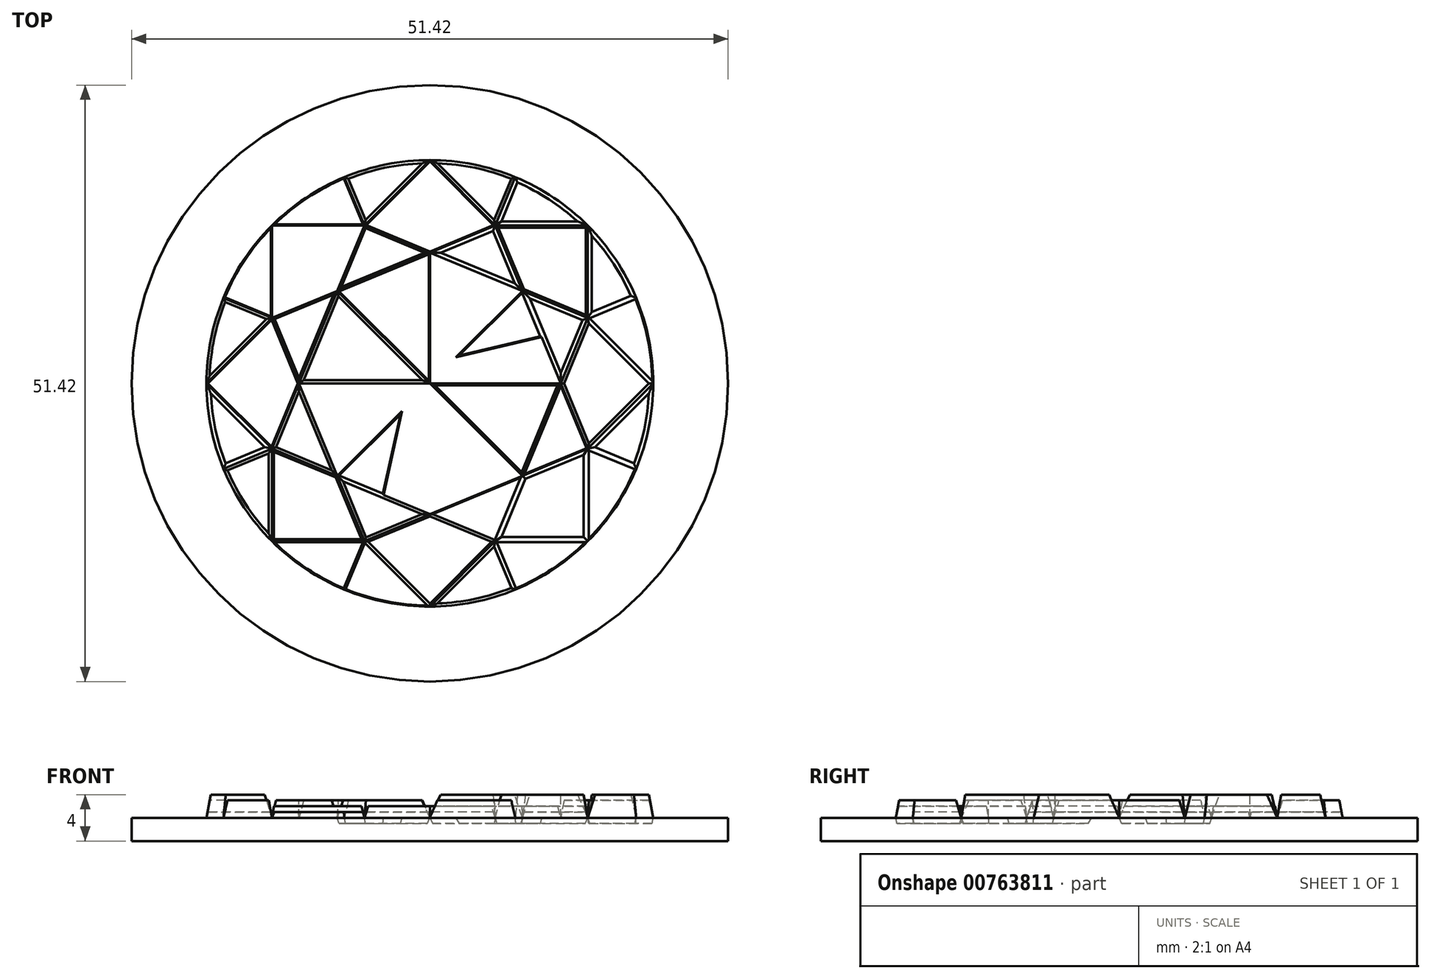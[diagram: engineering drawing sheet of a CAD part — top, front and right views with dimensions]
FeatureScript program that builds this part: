
annotation { "Feature Type Name" : "Feature", "Feature Type Description" : "" }
export const myFeature = defineFeature(function(context is Context, id is Id, definition is map)
    precondition{}
    {
        {
            var Q0;
            Q0=qCreatedBy(makeId("Top.planeOp"),FACE);
            var sketch = newSketch(context, id + "F0", { "sketchPlane" : qUnion([Q0])});
            skCircle(sketch, "E0", {"center": v(0, 0) * mm, "radius": 25.71 * mm});
            skSolve(sketch);
        }
        {
            var Q0;
            Q0 = qSketchRegion(id + "F0", true);
            extrude(context, id + "F1", {"entities" : qUnion([Q0]), "oppositeDirection" : true, "depth" : 2 * mm, "offsetDistance" : 25 * mm});
        }
        {
            var Q0;
            Q0=qCreatedBy(makeId("Top.planeOp"),FACE);
            var sketch = newSketch(context, id + "F2", { "sketchPlane" : qUnion([Q0])});
            skCircle(sketch, "E1", {"center": v(0, 0) * mm, "radius": 19.25 * mm});
            skCircle(sketch, "E2", {"center": v(0, 0) * mm, "radius": 25 * mm});
            skCircle(sketch, "E3.cCircle", {"center": v(0, 0) * mm, "radius": 14.73 * mm, "construction": true});
            skLineSegment(sketch, "E3.0", {"start": v(5.64, 13.61) * mm, "end": v(13.61, -5.64) * mm});
            skLineSegment(sketch, "E3.1", {"start": v(13.61, -5.64) * mm, "end": v(-5.64, -13.61) * mm});
            skLineSegment(sketch, "E3.2", {"start": v(-5.64, -13.61) * mm, "end": v(-13.61, 5.64) * mm});
            skLineSegment(sketch, "E3.3", {"start": v(-13.61, 5.64) * mm, "end": v(5.64, 13.61) * mm});
            skCircle(sketch, "E4.cCircle", {"center": v(0, 0) * mm, "radius": 19.25 * mm, "construction": true});
            skLineSegment(sketch, "E4.0", {"start": v(0, 19.25) * mm, "end": v(19.25, 0) * mm});
            skLineSegment(sketch, "E4.1", {"start": v(19.25, 0) * mm, "end": v(0, -19.25) * mm});
            skLineSegment(sketch, "E4.2", {"start": v(0, -19.25) * mm, "end": v(-19.25, 0) * mm});
            skLineSegment(sketch, "E4.3", {"start": v(-19.25, 0) * mm, "end": v(0, 19.25) * mm});
            skLineSegment(sketch, "E5.0", {"start": v(-13.61, 13.61) * mm, "end": v(13.61, 13.61) * mm});
            skLineSegment(sketch, "E5.1", {"start": v(13.61, 13.61) * mm, "end": v(13.61, -13.61) * mm});
            skLineSegment(sketch, "E5.2", {"start": v(13.61, -13.61) * mm, "end": v(-13.61, -13.61) * mm});
            skLineSegment(sketch, "E5.3", {"start": v(-13.61, -13.61) * mm, "end": v(-13.61, 13.61) * mm});
            skLineSegment(sketch, "E6.0", {"start": v(-5.64, 13.61) * mm, "end": v(13.61, 5.64) * mm});
            skLineSegment(sketch, "E6.1", {"start": v(13.61, 5.64) * mm, "end": v(5.64, -13.61) * mm});
            skLineSegment(sketch, "E6.2", {"start": v(5.64, -13.61) * mm, "end": v(-13.61, -5.64) * mm});
            skLineSegment(sketch, "E6.3", {"start": v(-13.61, -5.64) * mm, "end": v(-5.64, 13.61) * mm});
            skLineSegment(sketch, "E7", {"start": v(7.97, -7.97) * mm, "end": v(-7.97, 7.97) * mm});
            skLineSegment(sketch, "E8", {"start": v(-7.97, -7.97) * mm, "end": v(7.97, 7.97) * mm});
            skLineSegment(sketch, "E9", {"start": v(13.61, -5.64) * mm, "end": v(17.78, -7.37) * mm});
            skLineSegment(sketch, "E10", {"start": v(7.37, -17.78) * mm, "end": v(5.64, -13.61) * mm});
            skLineSegment(sketch, "E11", {"start": v(-7.37, -17.78) * mm, "end": v(-5.64, -13.61) * mm});
            skLineSegment(sketch, "E12", {"start": v(-13.61, -5.64) * mm, "end": v(-17.78, -7.37) * mm});
            skLineSegment(sketch, "E13", {"start": v(-13.61, 5.64) * mm, "end": v(-17.78, 7.37) * mm});
            skLineSegment(sketch, "E14", {"start": v(-5.64, 13.61) * mm, "end": v(-7.37, 17.78) * mm});
            skLineSegment(sketch, "E15", {"start": v(5.64, 13.61) * mm, "end": v(7.37, 17.78) * mm});
            skLineSegment(sketch, "E16", {"start": v(13.61, 5.64) * mm, "end": v(17.78, 7.37) * mm});
            skLineSegment(sketch, "E17", {"start": v(-2.39, -2.39) * mm, "end": v(-3.99, -9.63) * mm});
            skLineSegment(sketch, "E18", {"start": v(2.25, 2.25) * mm, "end": v(9.62, 3.99) * mm});
            skLineSegment(sketch, "E19", {"start": v(-25, 0) * mm, "end": v(-19.25, 0) * mm});
            skLineSegment(sketch, "E20", {"start": v(19.25, 0) * mm, "end": v(25, 0) * mm});
            skLineSegment(sketch, "E21", {"start": v(0, 0) * mm, "end": v(11.28, 0) * mm});
            skLineSegment(sketch, "E22", {"start": v(0, 0) * mm, "end": v(0, 11.28) * mm});
            skLineSegment(sketch, "E23", {"start": v(0, 0) * mm, "end": v(-11.28, 0) * mm});
            skSolve(sketch);
        }
        {
            var Q0;
            {var subQ3=sQuery(id+"F2.wireOp",EDGE,"E13");Q0=makeQuery(id+"F2.imprint","IMPRINT",FACE,{"disambiguationData":[TD([[makeQuery(id+"F2.imprint","IMPRINT",EDGE,{"derivedFrom":subQ3}),-1.0]])]});}
            var Q1;
            {var subQ3=sQuery(id+"F2.wireOp",EDGE,"E14");Q1=makeQuery(id+"F2.imprint","IMPRINT",FACE,{"disambiguationData":[TD([[makeQuery(id+"F2.imprint","IMPRINT",EDGE,{"derivedFrom":subQ3}),1.0]])]});}
            var Q2;
            {var subQ1=sQuery(id+"F2.wireOp",EDGE,"E4.0");var subQ3=sQuery(id+"F2.wireOp",EDGE,"E4.3");var subQ4=makeQuery(id+"F2.imprint","INTERSECT",VERTEX,{"derivedFrom":[sQuery(id+"F2.wireOp",EDGE,"E1"),subQ1,subQ3]});Q2=makeQuery(id+"F2.imprint","IMPRINT",FACE,{"disambiguationData":[TD([[makeQuery(id+"F2.imprint","IMPRINT",EDGE,{"disambiguationData":[TD([[subQ4,-1.0]])],"derivedFrom":subQ1}),-1.0]])]});}
            var Q3;
            {var subQ1=sQuery(id+"F2.wireOp",EDGE,"E3.3");var subQ3=sQuery(id+"F2.wireOp",EDGE,"E6.0");var subQ4=makeQuery(id+"F2.imprint","INTERSECT",VERTEX,{"derivedFrom":[subQ1,subQ3,sQuery(id+"F2.wireOp",EDGE,"E22")]});Q3=makeQuery(id+"F2.imprint","IMPRINT",FACE,{"disambiguationData":[TD([[makeQuery(id+"F2.imprint","IMPRINT",EDGE,{"disambiguationData":[TD([[subQ4,-1.0]])],"derivedFrom":subQ1}),1.0]])]});}
            var Q4;
            {var subQ3=sQuery(id+"F2.wireOp",EDGE,"E22");Q4=makeQuery(id+"F2.imprint","IMPRINT",FACE,{"disambiguationData":[TD([[makeQuery(id+"F2.imprint","IMPRINT",EDGE,{"derivedFrom":subQ3}),1.0]])]});}
            var Q5;
            {var subQ0=sQuery(id+"F2.wireOp",EDGE,"E3.1");var subQ3=sQuery(id+"F2.wireOp",EDGE,"E6.1");var subQ5=makeQuery(id+"F2.imprint","INTERSECT",VERTEX,{"derivedFrom":[subQ0,subQ3,sQuery(id+"F2.wireOp",EDGE,"E7")]});Q5=makeQuery(id+"F2.imprint","IMPRINT",FACE,{"disambiguationData":[TD([[makeQuery(id+"F2.imprint","IMPRINT",EDGE,{"disambiguationData":[TD([[subQ5,1.0]])],"derivedFrom":subQ3}),1.0]])]});}
            var Q6;
            {var subQ3=sQuery(id+"F2.wireOp",EDGE,"E11");Q6=makeQuery(id+"F2.imprint","IMPRINT",FACE,{"disambiguationData":[TD([[makeQuery(id+"F2.imprint","IMPRINT",EDGE,{"derivedFrom":subQ3}),1.0]])]});}
            var Q7;
            {var subQ1=sQuery(id+"F2.wireOp",EDGE,"E3.2");var subQ3=sQuery(id+"F2.wireOp",EDGE,"E6.3");var subQ4=makeQuery(id+"F2.imprint","INTERSECT",VERTEX,{"derivedFrom":[subQ1,subQ3,sQuery(id+"F2.wireOp",EDGE,"E23")]});Q7=makeQuery(id+"F2.imprint","IMPRINT",FACE,{"disambiguationData":[TD([[makeQuery(id+"F2.imprint","IMPRINT",EDGE,{"disambiguationData":[TD([[subQ4,-1.0]])],"derivedFrom":subQ1}),1.0]])]});}
            var Q8;
            {var subQ0=sQuery(id+"F2.wireOp",EDGE,"E4.3");var subQ1=sQuery(id+"F2.wireOp",EDGE,"E4.2");var subQ2=makeQuery(id+"F2.imprint","INTERSECT",VERTEX,{"derivedFrom":[sQuery(id+"F2.wireOp",EDGE,"E1"),subQ1,subQ0,sQuery(id+"F2.wireOp",EDGE,"E19")]});Q8=makeQuery(id+"F2.imprint","IMPRINT",FACE,{"disambiguationData":[TD([[makeQuery(id+"F2.imprint","IMPRINT",EDGE,{"disambiguationData":[TD([[subQ2,1.0]])],"derivedFrom":subQ1}),-1.0]])]});}
            extrude(context, id + "F3", {"entities" : qUnion([Q0, Q1, Q2, Q3, Q4, Q5, Q6, Q7, Q8]), "operationType" : NewBodyOperationType.ADD, "flatOperationType" : FlatOperationType.REMOVE, "depth" : 0.5 * mm, "offsetDistance" : 25 * mm, "hasDraft" : true, "draftAngle" : 10 * degree, "draftPullDirection" : true, "domain" : OperationDomain.MODEL});
        }
        {
            var Q0;
            {var subQ1=sQuery(id+"F2.wireOp",EDGE,"E3.1");var subQ3=sQuery(id+"F2.wireOp",EDGE,"E6.2");var subQ4=makeQuery(id+"F2.imprint","INTERSECT",VERTEX,{"derivedFrom":[subQ1,subQ3]});Q0=makeQuery(id+"F2.imprint","IMPRINT",FACE,{"disambiguationData":[TD([[makeQuery(id+"F2.imprint","IMPRINT",EDGE,{"disambiguationData":[TD([[subQ4,-1.0]])],"derivedFrom":subQ1}),1.0]])]});}
            var Q1;
            {var subQ0=sQuery(id+"F2.wireOp",EDGE,"E4.2");var subQ1=sQuery(id+"F2.wireOp",EDGE,"E4.1");var subQ2=makeQuery(id+"F2.imprint","INTERSECT",VERTEX,{"derivedFrom":[sQuery(id+"F2.wireOp",EDGE,"E1"),subQ1,subQ0]});Q1=makeQuery(id+"F2.imprint","IMPRINT",FACE,{"disambiguationData":[TD([[makeQuery(id+"F2.imprint","IMPRINT",EDGE,{"disambiguationData":[TD([[subQ2,1.0]])],"derivedFrom":subQ1}),-1.0]])]});}
            var Q2;
            {var subQ0=sQuery(id+"F2.wireOp",EDGE,"E5.2");var subQ3=sQuery(id+"F2.wireOp",EDGE,"E5.3");var subQ5=makeQuery(id+"F2.imprint","INTERSECT",VERTEX,{"derivedFrom":[sQuery(id+"F2.wireOp",EDGE,"E1"),subQ0,subQ3]});Q2=makeQuery(id+"F2.imprint","IMPRINT",FACE,{"disambiguationData":[TD([[makeQuery(id+"F2.imprint","IMPRINT",EDGE,{"disambiguationData":[TD([[subQ5,1.0]])],"derivedFrom":subQ0}),-1.0]])]});}
            var Q3;
            {var subQ1=sQuery(id+"F2.wireOp",EDGE,"E3.2");var subQ3=sQuery(id+"F2.wireOp",EDGE,"E6.2");var subQ4=makeQuery(id+"F2.imprint","INTERSECT",VERTEX,{"derivedFrom":[subQ1,subQ3,sQuery(id+"F2.wireOp",EDGE,"E8")]});Q3=makeQuery(id+"F2.imprint","IMPRINT",FACE,{"disambiguationData":[TD([[makeQuery(id+"F2.imprint","IMPRINT",EDGE,{"disambiguationData":[TD([[subQ4,1.0]])],"derivedFrom":subQ1}),1.0]])]});}
            var Q4;
            {var subQ3=sQuery(id+"F2.wireOp",EDGE,"E21");Q4=makeQuery(id+"F2.imprint","IMPRINT",FACE,{"disambiguationData":[TD([[makeQuery(id+"F2.imprint","IMPRINT",EDGE,{"derivedFrom":subQ3}),-1.0]])]});}
            var Q5;
            {var subQ0=sQuery(id+"F2.wireOp",EDGE,"E5.0");var subQ3=sQuery(id+"F2.wireOp",EDGE,"E5.1");var subQ5=makeQuery(id+"F2.imprint","INTERSECT",VERTEX,{"derivedFrom":[sQuery(id+"F2.wireOp",EDGE,"E1"),subQ0,subQ3]});Q5=makeQuery(id+"F2.imprint","IMPRINT",FACE,{"disambiguationData":[TD([[makeQuery(id+"F2.imprint","IMPRINT",EDGE,{"disambiguationData":[TD([[subQ5,1.0]])],"derivedFrom":subQ0}),-1.0]])]});}
            var Q6;
            {var subQ1=sQuery(id+"F2.wireOp",EDGE,"E3.0");var subQ3=sQuery(id+"F2.wireOp",EDGE,"E6.0");var subQ4=makeQuery(id+"F2.imprint","INTERSECT",VERTEX,{"derivedFrom":[subQ1,subQ3,sQuery(id+"F2.wireOp",EDGE,"E8")]});Q6=makeQuery(id+"F2.imprint","IMPRINT",FACE,{"disambiguationData":[TD([[makeQuery(id+"F2.imprint","IMPRINT",EDGE,{"disambiguationData":[TD([[subQ4,1.0]])],"derivedFrom":subQ1}),1.0]])]});}
            var Q7;
            {var subQ0=sQuery(id+"F2.wireOp",EDGE,"E6.3");var subQ1=sQuery(id+"F2.wireOp",EDGE,"E3.3");var subQ2=makeQuery(id+"F2.imprint","INTERSECT",VERTEX,{"derivedFrom":[subQ1,subQ0,sQuery(id+"F2.wireOp",EDGE,"E7")]});Q7=makeQuery(id+"F2.imprint","IMPRINT",FACE,{"disambiguationData":[TD([[makeQuery(id+"F2.imprint","IMPRINT",EDGE,{"disambiguationData":[TD([[subQ2,-1.0]])],"derivedFrom":subQ1}),1.0]])]});}
            var Q8;
            {var subQ0=sQuery(id+"F2.wireOp",EDGE,"E3.3");var subQ3=sQuery(id+"F2.wireOp",EDGE,"E6.3");var subQ5=makeQuery(id+"F2.imprint","INTERSECT",VERTEX,{"derivedFrom":[subQ0,subQ3,sQuery(id+"F2.wireOp",EDGE,"E7")]});Q8=makeQuery(id+"F2.imprint","IMPRINT",FACE,{"disambiguationData":[TD([[makeQuery(id+"F2.imprint","IMPRINT",EDGE,{"disambiguationData":[TD([[subQ5,1.0]])],"derivedFrom":subQ3}),1.0]])]});}
            extrude(context, id + "F4", {"entities" : qUnion([Q0, Q1, Q2, Q3, Q4, Q5, Q6, Q7, Q8]), "operationType" : NewBodyOperationType.ADD, "flatOperationType" : FlatOperationType.REMOVE, "depth" : 1 * mm, "offsetDistance" : 25 * mm, "hasDraft" : true, "draftAngle" : 10 * degree, "draftPullDirection" : true, "domain" : OperationDomain.MODEL});
        }
        {
            var Q0;
            {var subQ3=sQuery(id+"F2.wireOp",EDGE,"E23");Q0=makeQuery(id+"F2.imprint","IMPRINT",FACE,{"disambiguationData":[TD([[makeQuery(id+"F2.imprint","IMPRINT",EDGE,{"derivedFrom":subQ3}),-1.0]])]});}
            var Q1;
            {var subQ0=sQuery(id+"F2.wireOp",EDGE,"E6.2");var subQ1=sQuery(id+"F2.wireOp",EDGE,"E3.2");var subQ2=makeQuery(id+"F2.imprint","INTERSECT",VERTEX,{"derivedFrom":[subQ1,subQ0,sQuery(id+"F2.wireOp",EDGE,"E8")]});Q1=makeQuery(id+"F2.imprint","IMPRINT",FACE,{"disambiguationData":[TD([[makeQuery(id+"F2.imprint","IMPRINT",EDGE,{"disambiguationData":[TD([[subQ2,-1.0]])],"derivedFrom":subQ1}),1.0]])]});}
            var Q2;
            {var subQ3=sQuery(id+"F2.wireOp",EDGE,"E13");Q2=makeQuery(id+"F2.imprint","IMPRINT",FACE,{"disambiguationData":[TD([[makeQuery(id+"F2.imprint","IMPRINT",EDGE,{"derivedFrom":subQ3}),1.0]])]});}
            var Q3;
            {var subQ3=sQuery(id+"F2.wireOp",EDGE,"E12");Q3=makeQuery(id+"F2.imprint","IMPRINT",FACE,{"disambiguationData":[TD([[makeQuery(id+"F2.imprint","IMPRINT",EDGE,{"derivedFrom":subQ3}),1.0]])]});}
            var Q4;
            {var subQ3=sQuery(id+"F2.wireOp",EDGE,"E6.2");var subQ6=makeQuery(id+"F2.imprint","INTERSECT",VERTEX,{"derivedFrom":[subQ3,sQuery(id+"F2.wireOp",EDGE,"E17")]});Q4=makeQuery(id+"F2.imprint","IMPRINT",FACE,{"disambiguationData":[TD([[makeQuery(id+"F2.imprint","IMPRINT",EDGE,{"disambiguationData":[TD([[subQ6,1.0]])],"derivedFrom":subQ3}),1.0]])]});}
            var Q5;
            {var subQ3=sQuery(id+"F2.wireOp",EDGE,"E10");Q5=makeQuery(id+"F2.imprint","IMPRINT",FACE,{"disambiguationData":[TD([[makeQuery(id+"F2.imprint","IMPRINT",EDGE,{"derivedFrom":subQ3}),1.0]])]});}
            var Q6;
            {var subQ0=sQuery(id+"F2.wireOp",EDGE,"E4.1");var subQ1=sQuery(id+"F2.wireOp",EDGE,"E4.0");var subQ2=makeQuery(id+"F2.imprint","INTERSECT",VERTEX,{"derivedFrom":[sQuery(id+"F2.wireOp",EDGE,"E1"),subQ1,subQ0,sQuery(id+"F2.wireOp",EDGE,"E20")]});Q6=makeQuery(id+"F2.imprint","IMPRINT",FACE,{"disambiguationData":[TD([[makeQuery(id+"F2.imprint","IMPRINT",EDGE,{"disambiguationData":[TD([[subQ2,1.0]])],"derivedFrom":subQ1}),-1.0]])]});}
            var Q7;
            {var subQ1=sQuery(id+"F2.wireOp",EDGE,"E3.0");var subQ3=sQuery(id+"F2.wireOp",EDGE,"E6.1");var subQ4=makeQuery(id+"F2.imprint","INTERSECT",VERTEX,{"derivedFrom":[subQ1,subQ3,sQuery(id+"F2.wireOp",EDGE,"E21")]});Q7=makeQuery(id+"F2.imprint","IMPRINT",FACE,{"disambiguationData":[TD([[makeQuery(id+"F2.imprint","IMPRINT",EDGE,{"disambiguationData":[TD([[subQ4,-1.0]])],"derivedFrom":subQ1}),1.0]])]});}
            var Q8;
            {var subQ3=sQuery(id+"F2.wireOp",EDGE,"E14");Q8=makeQuery(id+"F2.imprint","IMPRINT",FACE,{"disambiguationData":[TD([[makeQuery(id+"F2.imprint","IMPRINT",EDGE,{"derivedFrom":subQ3}),-1.0]])]});}
            var Q9;
            {var subQ3=sQuery(id+"F2.wireOp",EDGE,"E15");Q9=makeQuery(id+"F2.imprint","IMPRINT",FACE,{"disambiguationData":[TD([[makeQuery(id+"F2.imprint","IMPRINT",EDGE,{"derivedFrom":subQ3}),1.0]])]});}
            extrude(context, id + "F5", {"entities" : qUnion([Q0, Q1, Q2, Q3, Q4, Q5, Q6, Q7, Q8, Q9]), "operationType" : NewBodyOperationType.ADD, "flatOperationType" : FlatOperationType.REMOVE, "depth" : 1.5 * mm, "offsetDistance" : 25 * mm, "hasDraft" : true, "draftAngle" : 10 * degree, "draftPullDirection" : true, "domain" : OperationDomain.MODEL});
        }
        {
            var Q0;
            {var subQ3=sQuery(id+"F2.wireOp",EDGE,"E15");Q0=makeQuery(id+"F2.imprint","IMPRINT",FACE,{"disambiguationData":[TD([[makeQuery(id+"F2.imprint","IMPRINT",EDGE,{"derivedFrom":subQ3}),-1.0]])]});}
            var Q1;
            {var subQ3=sQuery(id+"F2.wireOp",EDGE,"E16");Q1=makeQuery(id+"F2.imprint","IMPRINT",FACE,{"disambiguationData":[TD([[makeQuery(id+"F2.imprint","IMPRINT",EDGE,{"derivedFrom":subQ3}),1.0]])]});}
            var Q2;
            {var subQ1=sQuery(id+"F2.wireOp",EDGE,"E3.0");var subQ3=sQuery(id+"F2.wireOp",EDGE,"E6.0");var subQ4=makeQuery(id+"F2.imprint","INTERSECT",VERTEX,{"derivedFrom":[subQ1,subQ3,sQuery(id+"F2.wireOp",EDGE,"E8")]});Q2=makeQuery(id+"F2.imprint","IMPRINT",FACE,{"disambiguationData":[TD([[makeQuery(id+"F2.imprint","IMPRINT",EDGE,{"disambiguationData":[TD([[subQ4,1.0]])],"derivedFrom":subQ3}),1.0]])]});}
            var Q3;
            {var subQ1=sQuery(id+"F2.wireOp",EDGE,"E3.0");var subQ3=makeQuery(id+"F2.imprint","INTERSECT",VERTEX,{"derivedFrom":[subQ1,sQuery(id+"F2.wireOp",EDGE,"E18")]});Q3=makeQuery(id+"F2.imprint","IMPRINT",FACE,{"disambiguationData":[TD([[makeQuery(id+"F2.imprint","IMPRINT",EDGE,{"disambiguationData":[TD([[subQ3,1.0]])],"derivedFrom":subQ1}),1.0]])]});}
            var Q4;
            {var subQ3=sQuery(id+"F2.wireOp",EDGE,"E9");Q4=makeQuery(id+"F2.imprint","IMPRINT",FACE,{"disambiguationData":[TD([[makeQuery(id+"F2.imprint","IMPRINT",EDGE,{"derivedFrom":subQ3}),1.0]])]});}
            var Q5;
            {var subQ0=sQuery(id+"F2.wireOp",EDGE,"E5.1");var subQ3=sQuery(id+"F2.wireOp",EDGE,"E5.2");var subQ5=makeQuery(id+"F2.imprint","INTERSECT",VERTEX,{"derivedFrom":[sQuery(id+"F2.wireOp",EDGE,"E1"),subQ0,subQ3]});Q5=makeQuery(id+"F2.imprint","IMPRINT",FACE,{"disambiguationData":[TD([[makeQuery(id+"F2.imprint","IMPRINT",EDGE,{"disambiguationData":[TD([[subQ5,1.0]])],"derivedFrom":subQ0}),-1.0]])]});}
            var Q6;
            {var subQ1=sQuery(id+"F2.wireOp",EDGE,"E3.1");var subQ3=sQuery(id+"F2.wireOp",EDGE,"E6.1");var subQ4=makeQuery(id+"F2.imprint","INTERSECT",VERTEX,{"derivedFrom":[subQ1,subQ3,sQuery(id+"F2.wireOp",EDGE,"E7")]});Q6=makeQuery(id+"F2.imprint","IMPRINT",FACE,{"disambiguationData":[TD([[makeQuery(id+"F2.imprint","IMPRINT",EDGE,{"disambiguationData":[TD([[subQ4,1.0]])],"derivedFrom":subQ1}),1.0]])]});}
            var Q7;
            {var subQ3=sQuery(id+"F2.wireOp",EDGE,"E12");Q7=makeQuery(id+"F2.imprint","IMPRINT",FACE,{"disambiguationData":[TD([[makeQuery(id+"F2.imprint","IMPRINT",EDGE,{"derivedFrom":subQ3}),-1.0]])]});}
            extrude(context, id + "F6", {"entities" : qUnion([Q0, Q1, Q2, Q3, Q4, Q5, Q6, Q7]), "operationType" : NewBodyOperationType.ADD, "flatOperationType" : FlatOperationType.REMOVE, "depth" : 2 * mm, "offsetDistance" : 25 * mm, "hasDraft" : true, "draftAngle" : 10 * degree, "draftPullDirection" : true, "domain" : OperationDomain.MODEL});
        }
        {
            var Q0;
            {var subQ3=sQuery(id+"F2.wireOp",EDGE,"E18");Q0=makeQuery(id+"F2.imprint","IMPRINT",FACE,{"disambiguationData":[TD([[makeQuery(id+"F2.imprint","IMPRINT",EDGE,{"derivedFrom":subQ3}),1.0]])]});}
            var Q1;
            {var subQ3=sQuery(id+"F2.wireOp",EDGE,"E17");Q1=makeQuery(id+"F2.imprint","IMPRINT",FACE,{"disambiguationData":[TD([[makeQuery(id+"F2.imprint","IMPRINT",EDGE,{"derivedFrom":subQ3}),-1.0]])]});}
            var Q2;
            {var subQ3=sQuery(id+"F2.wireOp",EDGE,"E11");Q2=makeQuery(id+"F2.imprint","IMPRINT",FACE,{"disambiguationData":[TD([[makeQuery(id+"F2.imprint","IMPRINT",EDGE,{"derivedFrom":subQ3}),-1.0]])]});}
            var Q3;
            {var subQ1=sQuery(id+"F2.wireOp",EDGE,"E3.1");var subQ3=sQuery(id+"F2.wireOp",EDGE,"E6.2");var subQ4=makeQuery(id+"F2.imprint","INTERSECT",VERTEX,{"derivedFrom":[subQ1,subQ3]});Q3=makeQuery(id+"F2.imprint","IMPRINT",FACE,{"disambiguationData":[TD([[makeQuery(id+"F2.imprint","IMPRINT",EDGE,{"disambiguationData":[TD([[subQ4,1.0]])],"derivedFrom":subQ1}),1.0]])]});}
            var Q4;
            {var subQ3=sQuery(id+"F2.wireOp",EDGE,"E10");Q4=makeQuery(id+"F2.imprint","IMPRINT",FACE,{"disambiguationData":[TD([[makeQuery(id+"F2.imprint","IMPRINT",EDGE,{"derivedFrom":subQ3}),-1.0]])]});}
            var Q5;
            {var subQ3=sQuery(id+"F2.wireOp",EDGE,"E9");Q5=makeQuery(id+"F2.imprint","IMPRINT",FACE,{"disambiguationData":[TD([[makeQuery(id+"F2.imprint","IMPRINT",EDGE,{"derivedFrom":subQ3}),-1.0]])]});}
            var Q6;
            {var subQ3=sQuery(id+"F2.wireOp",EDGE,"E16");Q6=makeQuery(id+"F2.imprint","IMPRINT",FACE,{"disambiguationData":[TD([[makeQuery(id+"F2.imprint","IMPRINT",EDGE,{"derivedFrom":subQ3}),-1.0]])]});}
            extrude(context, id + "F7", {"entities" : qUnion([Q0, Q1, Q2, Q3, Q4, Q5, Q6]), "operationType" : NewBodyOperationType.REMOVE, "flatOperationType" : FlatOperationType.REMOVE, "oppositeDirection" : true, "depth" : 0.5 * mm, "offsetDistance" : 25 * mm, "hasDraft" : true, "draftAngle" : 10 * degree, "draftPullDirection" : true, "domain" : OperationDomain.MODEL});
        }
    });
